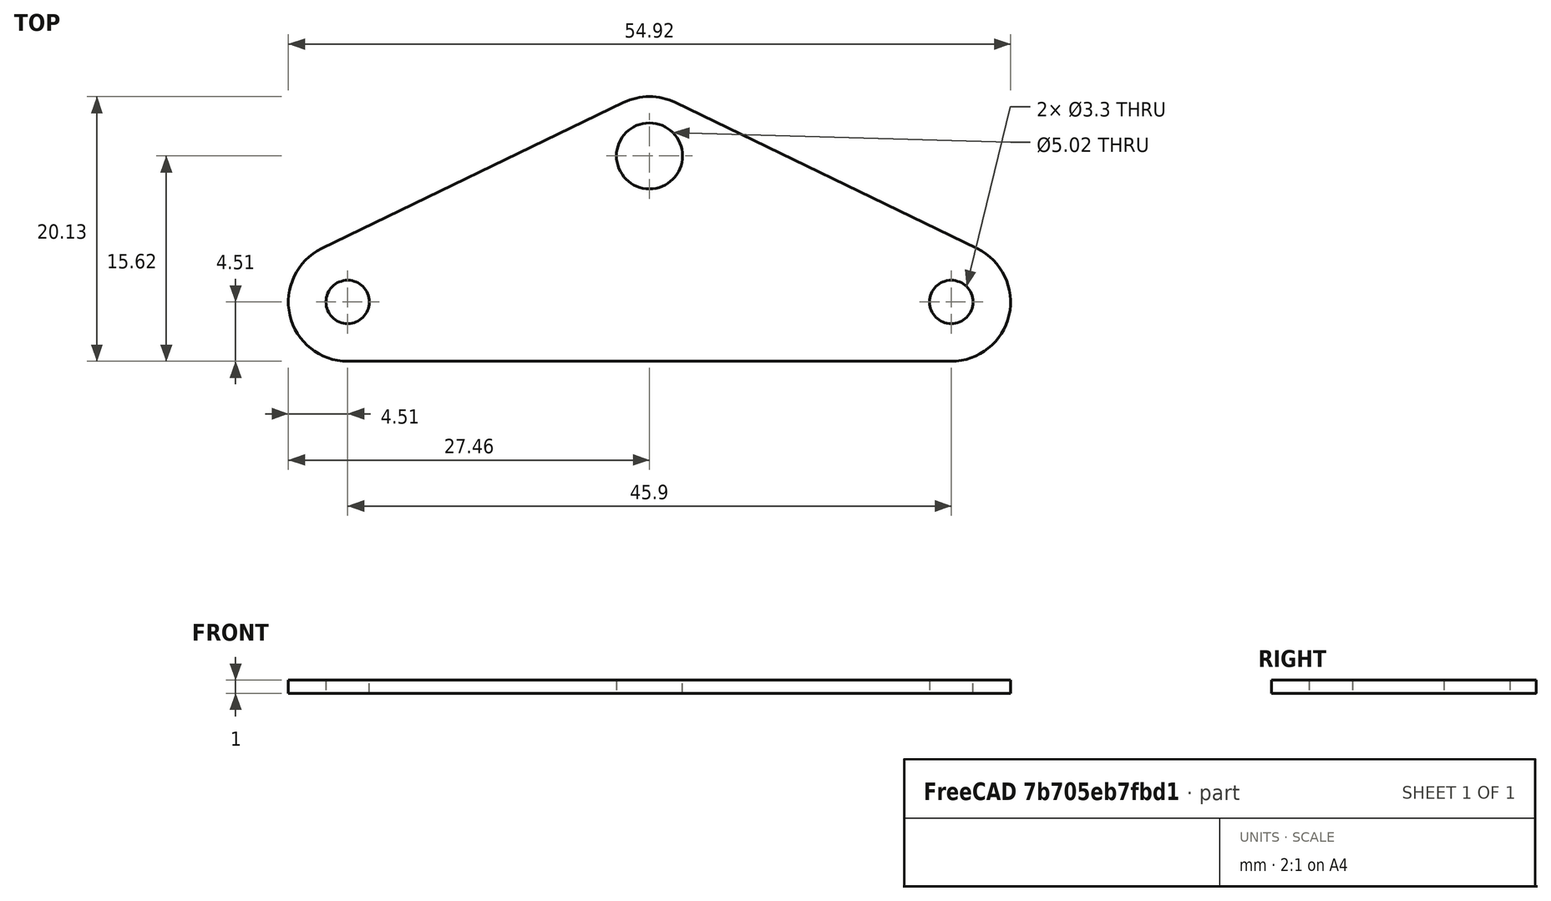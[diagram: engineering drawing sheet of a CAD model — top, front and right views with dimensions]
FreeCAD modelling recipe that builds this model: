
FCSTD DOCUMENT  (FreeCAD 0.19R24291 (Git))
Label: JL-30B500_fixture
License: All rights reserved
LicenseURL: http://en.wikipedia.org/wiki/All_rights_reserved
objects: Sketcher::SketchObject×1, PartDesign::Pad×1, PartDesign::Body×1
note: 4 computed .brp shape members not serialized (recipe doc carries the construction recipe); baked Part::Feature solids carry a one-line shape summary decoded from their .brp

FEATURE [Sketcher::SketchObject] Sketch
  FullyConstrained = false
  MapMode = 5
  Support = -> [XY_Plane]
  sketch-geometry (17):
    g0: Circle CenterX=-22.95 CenterY=0 CenterZ=0 NormalX=0 NormalY=0 NormalZ=1 AngleXU=0 Radius=1.65
    g1: Circle CenterX=22.95 CenterY=0 CenterZ=0 NormalX=0 NormalY=0 NormalZ=1 AngleXU=0 Radius=1.65
    g2: LineSegment StartX=0 StartY=0 StartZ=0 EndX=-21.3 EndY=0 EndZ=0
    g3: LineSegment StartX=0 StartY=0 StartZ=0 EndX=-24.6 EndY=0 EndZ=0
    g4: LineSegment StartX=0 StartY=0 StartZ=0 EndX=21.3 EndY=0 EndZ=0
    g5: Circle CenterX=0 CenterY=11.11 CenterZ=0 NormalX=0 NormalY=0 NormalZ=1 AngleXU=0 Radius=2.51
    g6: LineSegment StartX=0 StartY=0 StartZ=0 EndX=0 EndY=8.6 EndZ=0
    g7: GeomPoint X=0 Y=13.62 Z=0
    g8: GeomPoint X=-24.2934 Y=-0.958004 Z=0
    g9: ArcOfCircle CenterX=-22.95 CenterY=0 CenterZ=0 NormalX=0 NormalY=0 NormalZ=1 AngleXU=0 Radius=4.51 StartAngle=2.02164 EndAngle=4.71239
    g10: ArcOfCircle CenterX=0 CenterY=11.11 CenterZ=0 NormalX=0 NormalY=0 NormalZ=1 AngleXU=0 Radius=4.51 StartAngle=1.11995 EndAngle=2.02164
    g11: ArcOfCircle CenterX=22.95 CenterY=0 CenterZ=0 NormalX=0 NormalY=0 NormalZ=1 AngleXU=0 Radius=4.51 StartAngle=4.71238 EndAngle=7.40314
    g12: LineSegment StartX=1.96512 StartY=15.1694 StartZ=0 EndX=24.9151 EndY=4.05936 EndZ=0
    g13: LineSegment StartX=22.95 StartY=-4.51 StartZ=0 EndX=-22.95 EndY=-4.51 EndZ=0
    g14: LineSegment StartX=-24.9151 StartY=4.05936 StartZ=0 EndX=-1.96512 EndY=15.1694 EndZ=0
    g15: GeomPoint X=0 Y=13.62 Z=0
    g16: GeomPoint X=0 Y=15.62 Z=0
  constraints (45):
    c: PointOnObject(g1,g-1)
    c: Equal(g1,g0)
    c: Distance(g2) = 21.3
    c: PointOnObject(g3,g0)
    c: Distance(g3) = 24.6
    c: Coincident(g2,g-1)
    c: PointOnObject(g3,g-1)
    c: Coincident(g-1,g3)
    c: PointOnObject(g2,g0)
    c: Horizontal(g2)
    c: Coincident(g4,g-1)
    c: PointOnObject(g4,g1)
    c: Horizontal(g4)
    c: PointOnObject(g0,g3)
    c: Equal(g4,g2)
    c: PointOnObject(g5,g-2)
    c: Coincident(g6,g4)
    c: Vertical(g6)
    c: Distance(g6) = 8.6
    c: PointOnObject(g6,g5)
    c: Diameter(g5) = 5.02
    c: PointOnObject(g7,g5)
    c: PointOnObject(g8,g0)
    c: Coincident(g9,g0)
    c: Coincident(g10,g5)
    c: Coincident(g11,g1)
    c: Horizontal(g13)
    c: Coincident(g14,g10)
    c: Coincident(g10,g12)
    c: Coincident(g12,g11)
    c: Coincident(g13,g11)
    c: Coincident(g9,g13)
    c: Coincident(g9,g14)
    c: Tangent(g12,g10)
    c: Tangent(g14,g10)
    c: Tangent(g9,g14)
    c: Tangent(g9,g13)
    c: Tangent(g12,g11)
    c: Equal(g11,g10)
    c: Coincident(g15,g7)
    c: PointOnObject(g16,g10)
    c: PointOnObject(g16,g-2)
    c: PointOnObject(g7,g-2)
    c: DistanceY(g7,g16) = 2
    c: Tangent(g11,g13)
FEATURE [PartDesign::Pad] Pad
  Direction = (1,1,1)
  Length = 1
  Length2 = 100
  Profile = -> Sketch
  Type = 0
FEATURE [PartDesign::Body] Body
  Group = -> [Sketch,Pad]
  Origin = -> Origin
  Tip = -> Pad
